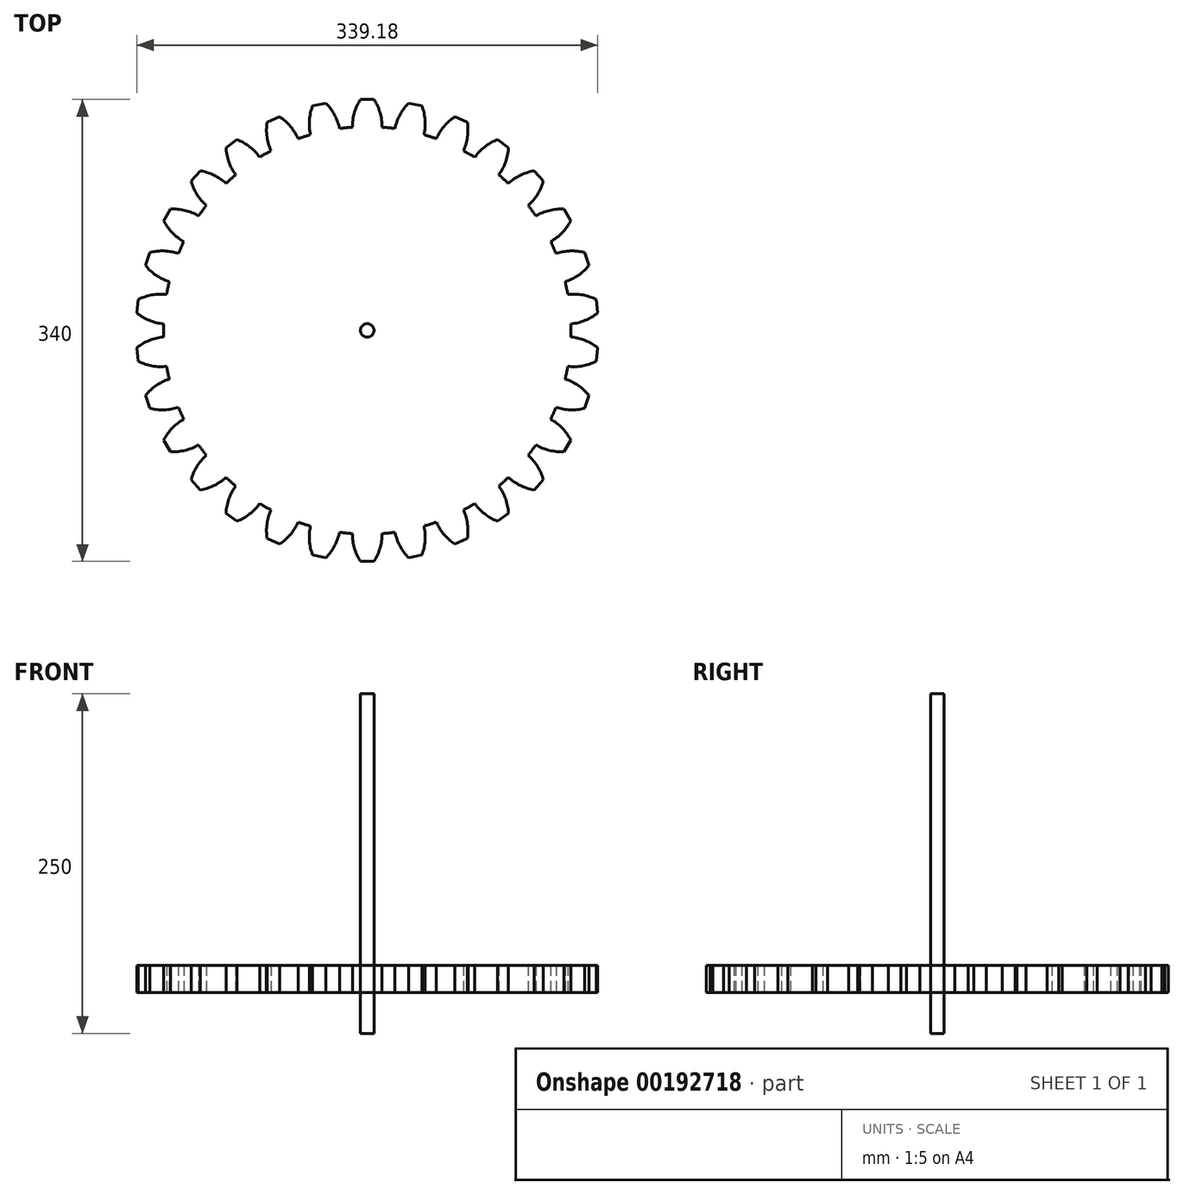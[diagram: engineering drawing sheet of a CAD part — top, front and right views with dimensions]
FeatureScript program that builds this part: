
annotation { "Feature Type Name" : "Feature", "Feature Type Description" : "" }
export const myFeature = defineFeature(function(context is Context, id is Id, definition is map)
    precondition{}
    {
        {
            var Q0;
            Q0=qCreatedBy(makeId("Top.planeOp"),FACE);
            var sketch = newSketch(context, id + "F0", { "sketchPlane" : qUnion([Q0])});
            skCircle(sketch, "E0", {"center": v(0, 0) * mm, "radius": 150 * mm});
            skLineSegment(sketch, "E1", {"start": v(0, 0) * mm, "end": v(0, 150) * mm, "construction": true});
            skLineSegment(sketch, "E2", {"start": v(0, 150) * mm, "end": v(0, 170) * mm});
            skLineSegment(sketch, "E3", {"start": v(0, 170) * mm, "end": v(-5, 170) * mm});
            skArc(sketch, "E4", {"start": v(-5, 170) * mm, "mid": v(-9.44, 160.23) * mm, "end": v(-10.89, 149.6) * mm});
            skLineSegment(sketch, "E5.MirrorCS", {"start": v(0, 170) * mm, "end": v(5, 170) * mm});
            skArc(sketch, "E6.MirrorCS", {"start": v(5, 170) * mm, "mid": v(9.44, 160.23) * mm, "end": v(10.89, 149.6) * mm});
            skArc(sketch, "E7.1.0", {"start": v(-40.24, 165.25) * mm, "mid": v(-42.55, 154.77) * mm, "end": v(-41.76, 144.07) * mm});
            skLineSegment(sketch, "E7.1.1", {"start": v(-35.34, 166.29) * mm, "end": v(-40.24, 165.25) * mm});
            skLineSegment(sketch, "E7.1.2", {"start": v(-35.34, 166.29) * mm, "end": v(-30.45, 167.32) * mm});
            skArc(sketch, "E7.1.3", {"start": v(-30.45, 167.32) * mm, "mid": v(-24.08, 158.7) * mm, "end": v(-20.45, 148.6) * mm});
            skArc(sketch, "E7.2.0", {"start": v(-73.71, 153.27) * mm, "mid": v(-73.8, 142.54) * mm, "end": v(-70.8, 132.24) * mm});
            skLineSegment(sketch, "E7.2.1", {"start": v(-69.15, 155.3) * mm, "end": v(-73.71, 153.27) * mm});
            skLineSegment(sketch, "E7.2.2", {"start": v(-69.15, 155.3) * mm, "end": v(-64.58, 157.34) * mm});
            skArc(sketch, "E7.2.3", {"start": v(-64.58, 157.34) * mm, "mid": v(-56.55, 150.22) * mm, "end": v(-50.9, 141.1) * mm});
            skArc(sketch, "E7.3.0", {"start": v(-103.97, 134.6) * mm, "mid": v(-101.82, 124.08) * mm, "end": v(-96.75, 114.63) * mm});
            skLineSegment(sketch, "E7.3.1", {"start": v(-99.92, 137.53) * mm, "end": v(-103.97, 134.6) * mm});
            skLineSegment(sketch, "E7.3.2", {"start": v(-99.92, 137.53) * mm, "end": v(-95.88, 140.47) * mm});
            skArc(sketch, "E7.3.3", {"start": v(-95.88, 140.47) * mm, "mid": v(-86.54, 135.18) * mm, "end": v(-79.13, 127.43) * mm});
            skArc(sketch, "E7.4.0", {"start": v(-129.68, 110.04) * mm, "mid": v(-125.4, 100.2) * mm, "end": v(-118.46, 92.01) * mm});
            skLineSegment(sketch, "E7.4.1", {"start": v(-126.33, 113.75) * mm, "end": v(-129.68, 110.04) * mm});
            skLineSegment(sketch, "E7.4.2", {"start": v(-126.33, 113.75) * mm, "end": v(-122.99, 117.47) * mm});
            skArc(sketch, "E7.4.3", {"start": v(-122.99, 117.47) * mm, "mid": v(-112.76, 114.24) * mm, "end": v(-103.9, 108.2) * mm});
            skArc(sketch, "E7.5.0", {"start": v(-149.72, 80.67) * mm, "mid": v(-143.49, 71.94) * mm, "end": v(-135, 65.37) * mm});
            skLineSegment(sketch, "E7.5.1", {"start": v(-147.22, 85) * mm, "end": v(-149.72, 80.67) * mm});
            skLineSegment(sketch, "E7.5.2", {"start": v(-147.22, 85) * mm, "end": v(-144.72, 89.33) * mm});
            skArc(sketch, "E7.5.3", {"start": v(-144.72, 89.33) * mm, "mid": v(-134.05, 88.3) * mm, "end": v(-124.12, 84.23) * mm});
            skArc(sketch, "E7.6.0", {"start": v(-163.22, 47.78) * mm, "mid": v(-155.31, 40.53) * mm, "end": v(-145.65, 35.87) * mm});
            skLineSegment(sketch, "E7.6.1", {"start": v(-161.68, 52.53) * mm, "end": v(-163.22, 47.78) * mm});
            skLineSegment(sketch, "E7.6.2", {"start": v(-161.68, 52.53) * mm, "end": v(-160.13, 57.29) * mm});
            skArc(sketch, "E7.6.3", {"start": v(-160.13, 57.29) * mm, "mid": v(-149.47, 58.5) * mm, "end": v(-138.92, 56.59) * mm});
            skArc(sketch, "E7.7.0", {"start": v(-169.6, 12.8) * mm, "mid": v(-160.34, 7.36) * mm, "end": v(-149.92, 4.8) * mm});
            skLineSegment(sketch, "E7.7.1", {"start": v(-169.07, 17.77) * mm, "end": v(-169.6, 12.8) * mm});
            skLineSegment(sketch, "E7.7.2", {"start": v(-169.07, 17.77) * mm, "end": v(-168.55, 22.74) * mm});
            skArc(sketch, "E7.7.3", {"start": v(-168.55, 22.74) * mm, "mid": v(-158.37, 26.14) * mm, "end": v(-147.65, 26.47) * mm});
            skArc(sketch, "E8.3.8.0", {"start": v(-168.55, -22.74) * mm, "mid": v(-158.37, -26.14) * mm, "end": v(-147.65, -26.47) * mm});
            skLineSegment(sketch, "E8.4.8.0", {"start": v(-169.07, -17.77) * mm, "end": v(-168.55, -22.74) * mm});
            skLineSegment(sketch, "E8.7.8.0", {"start": v(-169.07, -17.77) * mm, "end": v(-169.6, -12.8) * mm});
            skArc(sketch, "E8.10.8.0", {"start": v(-169.6, -12.8) * mm, "mid": v(-160.34, -7.36) * mm, "end": v(-149.92, -4.8) * mm});
            skArc(sketch, "E8.3.9.0", {"start": v(-160.13, -57.29) * mm, "mid": v(-149.47, -58.5) * mm, "end": v(-138.92, -56.59) * mm});
            skLineSegment(sketch, "E8.4.9.0", {"start": v(-161.68, -52.53) * mm, "end": v(-160.13, -57.29) * mm});
            skLineSegment(sketch, "E8.7.9.0", {"start": v(-161.68, -52.53) * mm, "end": v(-163.22, -47.78) * mm});
            skArc(sketch, "E8.10.9.0", {"start": v(-163.22, -47.78) * mm, "mid": v(-155.31, -40.53) * mm, "end": v(-145.65, -35.87) * mm});
            skArc(sketch, "E9.3.10.0", {"start": v(-144.72, -89.33) * mm, "mid": v(-134.05, -88.3) * mm, "end": v(-124.12, -84.23) * mm});
            skLineSegment(sketch, "E9.4.10.0", {"start": v(-147.22, -85) * mm, "end": v(-144.72, -89.33) * mm});
            skLineSegment(sketch, "E9.7.10.0", {"start": v(-147.22, -85) * mm, "end": v(-149.72, -80.67) * mm});
            skArc(sketch, "E9.10.10.0", {"start": v(-149.72, -80.67) * mm, "mid": v(-143.49, -71.94) * mm, "end": v(-135, -65.37) * mm});
            skArc(sketch, "E9.3.11.0", {"start": v(-122.99, -117.47) * mm, "mid": v(-112.76, -114.24) * mm, "end": v(-103.9, -108.2) * mm});
            skLineSegment(sketch, "E9.4.11.0", {"start": v(-126.33, -113.75) * mm, "end": v(-122.99, -117.47) * mm});
            skLineSegment(sketch, "E9.7.11.0", {"start": v(-126.33, -113.75) * mm, "end": v(-129.68, -110.04) * mm});
            skArc(sketch, "E9.10.11.0", {"start": v(-129.68, -110.04) * mm, "mid": v(-125.4, -100.2) * mm, "end": v(-118.46, -92.01) * mm});
            skArc(sketch, "E9.3.12.0", {"start": v(-95.88, -140.47) * mm, "mid": v(-86.54, -135.18) * mm, "end": v(-79.13, -127.43) * mm});
            skLineSegment(sketch, "E9.4.12.0", {"start": v(-99.92, -137.53) * mm, "end": v(-95.88, -140.47) * mm});
            skLineSegment(sketch, "E9.7.12.0", {"start": v(-99.92, -137.53) * mm, "end": v(-103.97, -134.6) * mm});
            skArc(sketch, "E9.10.12.0", {"start": v(-103.97, -134.6) * mm, "mid": v(-101.82, -124.08) * mm, "end": v(-96.75, -114.63) * mm});
            skArc(sketch, "E9.3.13.0", {"start": v(-64.58, -157.34) * mm, "mid": v(-56.55, -150.22) * mm, "end": v(-50.9, -141.1) * mm});
            skLineSegment(sketch, "E9.4.13.0", {"start": v(-69.15, -155.3) * mm, "end": v(-64.58, -157.34) * mm});
            skLineSegment(sketch, "E9.7.13.0", {"start": v(-69.15, -155.3) * mm, "end": v(-73.71, -153.27) * mm});
            skArc(sketch, "E9.10.13.0", {"start": v(-73.71, -153.27) * mm, "mid": v(-73.8, -142.54) * mm, "end": v(-70.8, -132.24) * mm});
            skArc(sketch, "E9.3.14.0", {"start": v(-30.45, -167.32) * mm, "mid": v(-24.08, -158.7) * mm, "end": v(-20.45, -148.6) * mm});
            skLineSegment(sketch, "E9.4.14.0", {"start": v(-35.34, -166.29) * mm, "end": v(-30.45, -167.32) * mm});
            skLineSegment(sketch, "E9.7.14.0", {"start": v(-35.34, -166.29) * mm, "end": v(-40.24, -165.25) * mm});
            skArc(sketch, "E9.10.14.0", {"start": v(-40.24, -165.25) * mm, "mid": v(-42.55, -154.77) * mm, "end": v(-41.76, -144.07) * mm});
            skArc(sketch, "E10.3.15.0", {"start": v(5, -170) * mm, "mid": v(9.44, -160.23) * mm, "end": v(10.89, -149.6) * mm});
            skLineSegment(sketch, "E10.4.15.0", {"start": v(0, -170) * mm, "end": v(5, -170) * mm});
            skLineSegment(sketch, "E10.7.15.0", {"start": v(0, -170) * mm, "end": v(-5, -170) * mm});
            skArc(sketch, "E10.10.15.0", {"start": v(-5, -170) * mm, "mid": v(-9.44, -160.23) * mm, "end": v(-10.89, -149.6) * mm});
            skArc(sketch, "E10.3.16.0", {"start": v(40.24, -165.25) * mm, "mid": v(42.55, -154.77) * mm, "end": v(41.76, -144.07) * mm});
            skLineSegment(sketch, "E10.4.16.0", {"start": v(35.34, -166.29) * mm, "end": v(40.24, -165.25) * mm});
            skLineSegment(sketch, "E10.7.16.0", {"start": v(35.34, -166.29) * mm, "end": v(30.45, -167.32) * mm});
            skArc(sketch, "E10.10.16.0", {"start": v(30.45, -167.32) * mm, "mid": v(24.08, -158.7) * mm, "end": v(20.45, -148.6) * mm});
            skArc(sketch, "E10.3.17.0", {"start": v(73.71, -153.27) * mm, "mid": v(73.8, -142.54) * mm, "end": v(70.8, -132.24) * mm});
            skLineSegment(sketch, "E10.4.17.0", {"start": v(69.15, -155.3) * mm, "end": v(73.71, -153.27) * mm});
            skLineSegment(sketch, "E10.7.17.0", {"start": v(69.15, -155.3) * mm, "end": v(64.58, -157.34) * mm});
            skArc(sketch, "E10.10.17.0", {"start": v(64.58, -157.34) * mm, "mid": v(56.55, -150.22) * mm, "end": v(50.9, -141.1) * mm});
            skArc(sketch, "E10.3.18.0", {"start": v(103.97, -134.6) * mm, "mid": v(101.82, -124.08) * mm, "end": v(96.75, -114.63) * mm});
            skLineSegment(sketch, "E10.4.18.0", {"start": v(99.92, -137.53) * mm, "end": v(103.97, -134.6) * mm});
            skLineSegment(sketch, "E10.7.18.0", {"start": v(99.92, -137.53) * mm, "end": v(95.88, -140.47) * mm});
            skArc(sketch, "E10.10.18.0", {"start": v(95.88, -140.47) * mm, "mid": v(86.54, -135.18) * mm, "end": v(79.13, -127.43) * mm});
            skArc(sketch, "E10.3.19.0", {"start": v(129.68, -110.04) * mm, "mid": v(125.4, -100.2) * mm, "end": v(118.46, -92.01) * mm});
            skLineSegment(sketch, "E10.4.19.0", {"start": v(126.33, -113.75) * mm, "end": v(129.68, -110.04) * mm});
            skLineSegment(sketch, "E10.7.19.0", {"start": v(126.33, -113.75) * mm, "end": v(122.99, -117.47) * mm});
            skArc(sketch, "E10.10.19.0", {"start": v(122.99, -117.47) * mm, "mid": v(112.76, -114.24) * mm, "end": v(103.9, -108.2) * mm});
            skArc(sketch, "E10.3.20.0", {"start": v(149.72, -80.67) * mm, "mid": v(143.49, -71.94) * mm, "end": v(135, -65.37) * mm});
            skLineSegment(sketch, "E10.4.20.0", {"start": v(147.22, -85) * mm, "end": v(149.72, -80.67) * mm});
            skLineSegment(sketch, "E10.7.20.0", {"start": v(147.22, -85) * mm, "end": v(144.72, -89.33) * mm});
            skArc(sketch, "E10.10.20.0", {"start": v(144.72, -89.33) * mm, "mid": v(134.05, -88.3) * mm, "end": v(124.12, -84.23) * mm});
            skArc(sketch, "E10.3.21.0", {"start": v(163.22, -47.78) * mm, "mid": v(155.31, -40.53) * mm, "end": v(145.65, -35.87) * mm});
            skLineSegment(sketch, "E10.4.21.0", {"start": v(161.68, -52.53) * mm, "end": v(163.22, -47.78) * mm});
            skLineSegment(sketch, "E10.7.21.0", {"start": v(161.68, -52.53) * mm, "end": v(160.13, -57.29) * mm});
            skArc(sketch, "E10.10.21.0", {"start": v(160.13, -57.29) * mm, "mid": v(149.47, -58.5) * mm, "end": v(138.92, -56.59) * mm});
            skArc(sketch, "E10.3.22.0", {"start": v(169.6, -12.8) * mm, "mid": v(160.34, -7.36) * mm, "end": v(149.92, -4.8) * mm});
            skLineSegment(sketch, "E10.4.22.0", {"start": v(169.07, -17.77) * mm, "end": v(169.6, -12.8) * mm});
            skLineSegment(sketch, "E10.7.22.0", {"start": v(169.07, -17.77) * mm, "end": v(168.55, -22.74) * mm});
            skArc(sketch, "E10.10.22.0", {"start": v(168.55, -22.74) * mm, "mid": v(158.37, -26.14) * mm, "end": v(147.65, -26.47) * mm});
            skArc(sketch, "E10.3.23.0", {"start": v(168.55, 22.74) * mm, "mid": v(158.37, 26.14) * mm, "end": v(147.65, 26.47) * mm});
            skLineSegment(sketch, "E10.4.23.0", {"start": v(169.07, 17.77) * mm, "end": v(168.55, 22.74) * mm});
            skLineSegment(sketch, "E10.7.23.0", {"start": v(169.07, 17.77) * mm, "end": v(169.6, 12.8) * mm});
            skArc(sketch, "E10.10.23.0", {"start": v(169.6, 12.8) * mm, "mid": v(160.34, 7.36) * mm, "end": v(149.92, 4.8) * mm});
            skArc(sketch, "E10.3.24.0", {"start": v(160.13, 57.29) * mm, "mid": v(149.47, 58.5) * mm, "end": v(138.92, 56.59) * mm});
            skLineSegment(sketch, "E10.4.24.0", {"start": v(161.68, 52.53) * mm, "end": v(160.13, 57.29) * mm});
            skLineSegment(sketch, "E10.7.24.0", {"start": v(161.68, 52.53) * mm, "end": v(163.22, 47.78) * mm});
            skArc(sketch, "E10.10.24.0", {"start": v(163.22, 47.78) * mm, "mid": v(155.31, 40.53) * mm, "end": v(145.65, 35.87) * mm});
            skArc(sketch, "E10.3.25.0", {"start": v(144.72, 89.33) * mm, "mid": v(134.05, 88.3) * mm, "end": v(124.12, 84.23) * mm});
            skLineSegment(sketch, "E10.4.25.0", {"start": v(147.22, 85) * mm, "end": v(144.72, 89.33) * mm});
            skLineSegment(sketch, "E10.7.25.0", {"start": v(147.22, 85) * mm, "end": v(149.72, 80.67) * mm});
            skArc(sketch, "E10.10.25.0", {"start": v(149.72, 80.67) * mm, "mid": v(143.49, 71.94) * mm, "end": v(135, 65.37) * mm});
            skArc(sketch, "E10.3.26.0", {"start": v(122.99, 117.47) * mm, "mid": v(112.76, 114.24) * mm, "end": v(103.9, 108.2) * mm});
            skLineSegment(sketch, "E10.4.26.0", {"start": v(126.33, 113.75) * mm, "end": v(122.99, 117.47) * mm});
            skLineSegment(sketch, "E10.7.26.0", {"start": v(126.33, 113.75) * mm, "end": v(129.68, 110.04) * mm});
            skArc(sketch, "E10.10.26.0", {"start": v(129.68, 110.04) * mm, "mid": v(125.4, 100.2) * mm, "end": v(118.46, 92.01) * mm});
            skArc(sketch, "E10.3.27.0", {"start": v(95.88, 140.47) * mm, "mid": v(86.54, 135.18) * mm, "end": v(79.13, 127.43) * mm});
            skLineSegment(sketch, "E10.4.27.0", {"start": v(99.92, 137.53) * mm, "end": v(95.88, 140.47) * mm});
            skLineSegment(sketch, "E10.7.27.0", {"start": v(99.92, 137.53) * mm, "end": v(103.97, 134.6) * mm});
            skArc(sketch, "E10.10.27.0", {"start": v(103.97, 134.6) * mm, "mid": v(101.82, 124.08) * mm, "end": v(96.75, 114.63) * mm});
            skArc(sketch, "E10.3.28.0", {"start": v(64.58, 157.34) * mm, "mid": v(56.55, 150.22) * mm, "end": v(50.9, 141.1) * mm});
            skLineSegment(sketch, "E10.4.28.0", {"start": v(69.15, 155.3) * mm, "end": v(64.58, 157.34) * mm});
            skLineSegment(sketch, "E10.7.28.0", {"start": v(69.15, 155.3) * mm, "end": v(73.71, 153.27) * mm});
            skArc(sketch, "E10.10.28.0", {"start": v(73.71, 153.27) * mm, "mid": v(73.8, 142.54) * mm, "end": v(70.8, 132.24) * mm});
            skArc(sketch, "E10.3.29.0", {"start": v(30.45, 167.32) * mm, "mid": v(24.08, 158.7) * mm, "end": v(20.45, 148.6) * mm});
            skLineSegment(sketch, "E10.4.29.0", {"start": v(35.34, 166.29) * mm, "end": v(30.45, 167.32) * mm});
            skLineSegment(sketch, "E10.7.29.0", {"start": v(35.34, 166.29) * mm, "end": v(40.24, 165.25) * mm});
            skArc(sketch, "E10.10.29.0", {"start": v(40.24, 165.25) * mm, "mid": v(42.55, 154.77) * mm, "end": v(41.76, 144.07) * mm});
            skSolve(sketch);
        }
        {
            var Q0;
            Q0=qSketchRegion(id+"F0",true);
            extrude(context, id + "F1", {"entities" : qUnion([Q0]), "depth" : 20 * mm});
        }
        {
            var Q0;
            Q0=makeQuery(id+"F1.opExtrude","CAP_FACE",FACE,{"disambiguationData":[OSD([sQuery(id+"F0.wireOp",EDGE,"E0"),sQuery(id+"F0.wireOp",EDGE,"E3"),sQuery(id+"F0.wireOp",EDGE,"E4"),sQuery(id+"F0.wireOp",EDGE,"E5.MirrorCS"),sQuery(id+"F0.wireOp",EDGE,"E6.MirrorCS"),sQuery(id+"F0.wireOp",EDGE,"E7.1.0"),sQuery(id+"F0.wireOp",EDGE,"E7.1.1"),sQuery(id+"F0.wireOp",EDGE,"E7.1.2"),sQuery(id+"F0.wireOp",EDGE,"E7.1.3"),sQuery(id+"F0.wireOp",EDGE,"E7.2.0"),sQuery(id+"F0.wireOp",EDGE,"E7.2.1"),sQuery(id+"F0.wireOp",EDGE,"E7.2.2"),sQuery(id+"F0.wireOp",EDGE,"E7.2.3"),sQuery(id+"F0.wireOp",EDGE,"E7.3.0"),sQuery(id+"F0.wireOp",EDGE,"E7.3.1"),sQuery(id+"F0.wireOp",EDGE,"E7.3.2"),sQuery(id+"F0.wireOp",EDGE,"E7.3.3"),sQuery(id+"F0.wireOp",EDGE,"E7.4.0"),sQuery(id+"F0.wireOp",EDGE,"E7.4.1"),sQuery(id+"F0.wireOp",EDGE,"E7.4.2"),sQuery(id+"F0.wireOp",EDGE,"E7.4.3"),sQuery(id+"F0.wireOp",EDGE,"E7.5.0"),sQuery(id+"F0.wireOp",EDGE,"E7.5.1"),sQuery(id+"F0.wireOp",EDGE,"E7.5.2"),sQuery(id+"F0.wireOp",EDGE,"E7.5.3"),sQuery(id+"F0.wireOp",EDGE,"E7.6.0"),sQuery(id+"F0.wireOp",EDGE,"E7.6.1"),sQuery(id+"F0.wireOp",EDGE,"E7.6.2"),sQuery(id+"F0.wireOp",EDGE,"E7.6.3"),sQuery(id+"F0.wireOp",EDGE,"E7.7.0"),sQuery(id+"F0.wireOp",EDGE,"E7.7.1"),sQuery(id+"F0.wireOp",EDGE,"E7.7.2"),sQuery(id+"F0.wireOp",EDGE,"E7.7.3"),sQuery(id+"F0.wireOp",EDGE,"E7.8.0"),sQuery(id+"F0.wireOp",EDGE,"E7.8.1"),sQuery(id+"F0.wireOp",EDGE,"E7.8.2"),sQuery(id+"F0.wireOp",EDGE,"E7.8.3"),sQuery(id+"F0.wireOp",EDGE,"E7.9.0"),sQuery(id+"F0.wireOp",EDGE,"E7.9.1"),sQuery(id+"F0.wireOp",EDGE,"E7.9.2"),sQuery(id+"F0.wireOp",EDGE,"E7.9.3"),sQuery(id+"F0.wireOp",EDGE,"E7.10.0"),sQuery(id+"F0.wireOp",EDGE,"E7.10.1"),sQuery(id+"F0.wireOp",EDGE,"E7.10.2"),sQuery(id+"F0.wireOp",EDGE,"E7.10.3"),sQuery(id+"F0.wireOp",EDGE,"E7.11.0"),sQuery(id+"F0.wireOp",EDGE,"E7.11.1"),sQuery(id+"F0.wireOp",EDGE,"E7.11.2"),sQuery(id+"F0.wireOp",EDGE,"E7.11.3"),sQuery(id+"F0.wireOp",EDGE,"E7.12.0"),sQuery(id+"F0.wireOp",EDGE,"E7.12.1"),sQuery(id+"F0.wireOp",EDGE,"E7.12.2"),sQuery(id+"F0.wireOp",EDGE,"E7.12.3"),sQuery(id+"F0.wireOp",EDGE,"E7.13.0"),sQuery(id+"F0.wireOp",EDGE,"E7.13.1"),sQuery(id+"F0.wireOp",EDGE,"E7.13.2"),sQuery(id+"F0.wireOp",EDGE,"E7.13.3"),sQuery(id+"F0.wireOp",EDGE,"E7.14.0"),sQuery(id+"F0.wireOp",EDGE,"E7.14.1"),sQuery(id+"F0.wireOp",EDGE,"E7.14.2"),sQuery(id+"F0.wireOp",EDGE,"E7.14.3"),sQuery(id+"F0.wireOp",EDGE,"E7.15.0"),sQuery(id+"F0.wireOp",EDGE,"E7.15.1"),sQuery(id+"F0.wireOp",EDGE,"E7.15.2"),sQuery(id+"F0.wireOp",EDGE,"E7.15.3")])],"isStart":false});
            var sketch = newSketch(context, id + "F2", { "sketchPlane" : qUnion([Q0])});
            skCircle(sketch, "E11", {"center": v(0, 0) * mm, "radius": 5 * mm});
            skSolve(sketch);
        }
        {
            var Q0;
            Q0=qSketchRegion(id+"F2",true);
            extrude(context, id + "F3", {"entities" : qUnion([Q0]), "operationType" : NewBodyOperationType.ADD, "depth" : 200 * mm, "hasSecondDirection" : true, "secondDirectionOppositeDirection" : true, "secondDirectionDepth" : 50 * mm});
        }
    });
